# Revit family: Paper_Towel_Dispenser-Surface_Mounted-Bobrick-ClassicSeries-B-2974.rfaxxx
name_source: partatom
category: Specialty Equipment
units: mm (PartAtom-declared; Revit-internal decimal feet)

## family parameters
Cut with Voids When Loaded = Yes
Host = Face
OmniClass Number = 23.40.20.21.17
OmniClass Title = Paper Towel Dispensers, Disposal Units
Part Type = Normal
Room Calculation Point = No
Round Connector Dimension = Use Diameter
Shared = Yes

## types (1)
- B-2974
    3944-152 Folded Towel Dispenser Module = No
    3961-50 (Mechanical) Universal Roll Towel Dispenser Module = No
    3974-57 AC External Adapter (6V) = No
    ADA Compliant = Yes
    ADA/ICC = Yes
    Assembly Code = C1030200
    Battery Operated = Yes
    CBC = No
    Cabinet Material = Stainless Steel-Bobrick-Satin
    Default Elevation = 0"
    Description = Automatic, Universal Surface-Mounted Roll Towel Dispenser Equipped with LED Light
    Door Material = Stainless Steel-Bobrick-Satin
    Height = 15 1/2"
    Installation Type = Wall Mounted
    Manufacturer = Bobrick
    Material = Stainless Steel-Bobrick-Satin
    Model = B-2974
    Mounting Height = 60"
    Mounting Height Constraint = 63 1/2"
    Operation = Electronic Sensor
    Product Page URL = https://www.bobrick.com
    Revised Date = 01/11/2023
    URL = http://www.bobrick.com
    Width = 12 5/8"

## geometry (parser evidence)
native form markers: Sweep x2
no freeform markers — native parametric forms only
